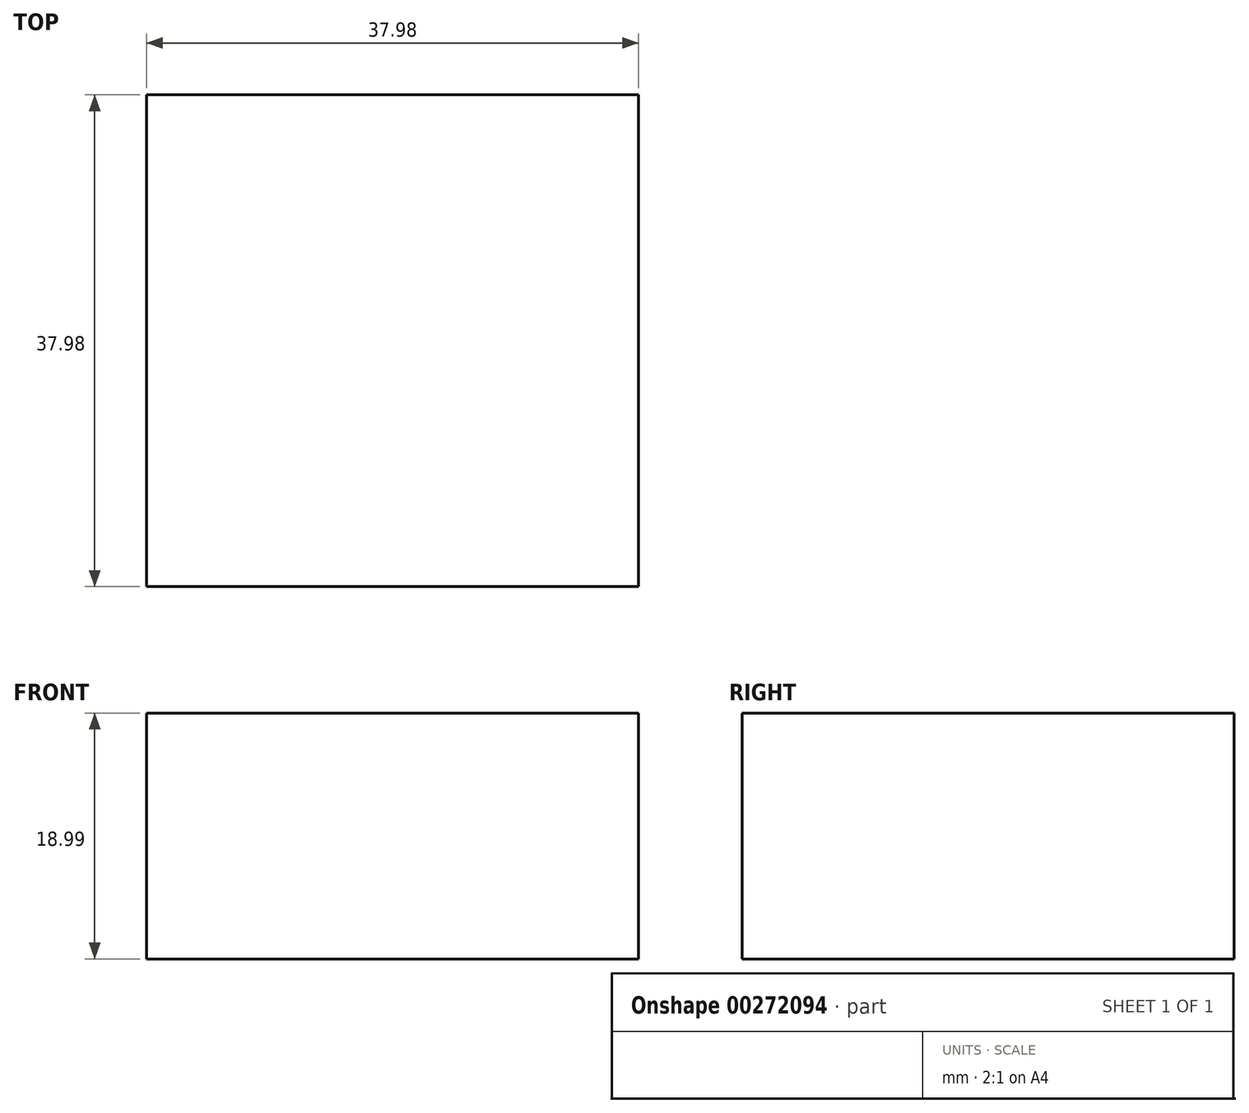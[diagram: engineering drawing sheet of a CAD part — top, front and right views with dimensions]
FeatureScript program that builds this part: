
annotation { "Feature Type Name" : "Feature", "Feature Type Description" : "" }
export const myFeature = defineFeature(function(context is Context, id is Id, definition is map)
    precondition{}
    {
        {
            var Q0;
            Q0=qCreatedBy(makeId("Top.planeOp"),FACE);
            var sketch = newSketch(context, id + "F0", { "sketchPlane" : qUnion([Q0])});
            skLineSegment(sketch, "E0.bottom", {"start": v(-18.99, 20.64) * mm, "end": v(18.99, 20.64) * mm});
            skLineSegment(sketch, "E0.top", {"start": v(-18.99, -17.34) * mm, "end": v(18.99, -17.34) * mm});
            skLineSegment(sketch, "E0.left", {"start": v(-18.99, 20.64) * mm, "end": v(-18.99, -17.34) * mm});
            skLineSegment(sketch, "E0.right", {"start": v(18.99, 20.64) * mm, "end": v(18.99, -17.34) * mm});
            skPoint(sketch, "E0.middle", {"position": v(0, 1.65) * mm});
            skSolve(sketch);
        }
        {
            var Q0;
            Q0=makeQuery(id+"F0.imprint","IMPRINT",FACE,{"disambiguationData":[TD([[makeQuery(id+"F0.imprint","IMPRINT",EDGE,{"derivedFrom":sQuery(id+"F0.wireOp",EDGE,"E0.bottom")}),-1.0]])]});
            extrude(context, id + "F1", {"entities" : qUnion([Q0]), "depth" : 18.99 * mm});
        }
    });
